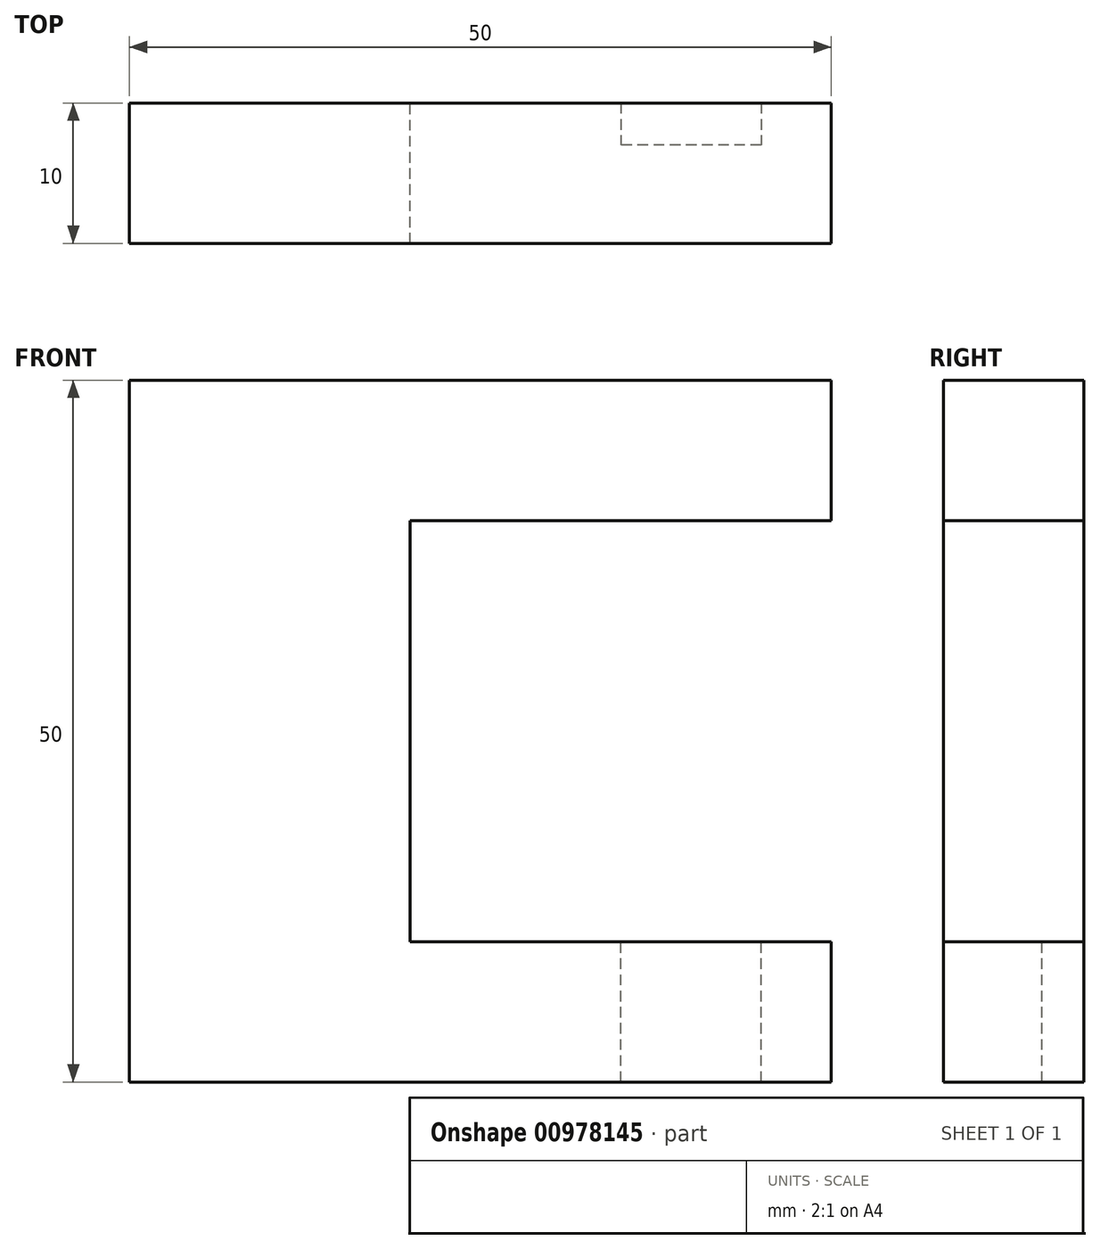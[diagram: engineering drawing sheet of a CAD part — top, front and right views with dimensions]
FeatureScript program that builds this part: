
annotation { "Feature Type Name" : "Feature", "Feature Type Description" : "" }
export const myFeature = defineFeature(function(context is Context, id is Id, definition is map)
    precondition{}
    {
        {
            var Q0;
            Q0=qCreatedBy(makeId("Front.planeOp"),FACE);
            var sketch = newSketch(context, id + "F0", { "sketchPlane" : qUnion([Q0])});
            skLineSegment(sketch, "E0.bottom", {"start": v(0, 0) * mm, "end": v(20, 0) * mm});
            skLineSegment(sketch, "E0.top", {"start": v(0, 50) * mm, "end": v(20, 50) * mm});
            skLineSegment(sketch, "E0.left", {"start": v(0, 0) * mm, "end": v(0, 50) * mm});
            skLineSegment(sketch, "E0.right", {"start": v(20, 10) * mm, "end": v(20, 40) * mm});
            skLineSegment(sketch, "E1.bottom", {"start": v(20, 0) * mm, "end": v(50, 0) * mm});
            skLineSegment(sketch, "E1.top", {"start": v(20, 10) * mm, "end": v(50, 10) * mm});
            skLineSegment(sketch, "E1.right", {"start": v(50, 0) * mm, "end": v(50, 10) * mm});
            skLineSegment(sketch, "E2.bottom", {"start": v(20, 50) * mm, "end": v(50, 50) * mm});
            skLineSegment(sketch, "E2.top", {"start": v(20, 40) * mm, "end": v(50, 40) * mm});
            skLineSegment(sketch, "E2.right", {"start": v(50, 50) * mm, "end": v(50, 40) * mm});
            skSolve(sketch);
        }
        {
            var Q0;
            Q0 = qSketchRegion(id + "F0", true);
            extrude(context, id + "F1", {"entities" : qUnion([Q0]), "depth" : 10 * mm, "offsetDistance" : 25 * mm});
        }
        {
            var Q0;
            Q0=makeQuery(id+"F1.opExtrude","SWEPT_FACE",FACE,{"disambiguationData":[OSD([sQuery(id+"F0.wireOp",EDGE,"E1.top")])]});
            var sketch = newSketch(context, id + "F2", { "sketchPlane" : qUnion([Q0])});
            skLineSegment(sketch, "E3.bottom", {"start": v(45, 0) * mm, "end": v(35, 0) * mm});
            skLineSegment(sketch, "E3.top", {"start": v(45, -3) * mm, "end": v(35, -3) * mm});
            skLineSegment(sketch, "E3.left", {"start": v(45, 0) * mm, "end": v(45, -3) * mm});
            skLineSegment(sketch, "E3.right", {"start": v(35, 0) * mm, "end": v(35, -3) * mm});
            skSolve(sketch);
        }
        {
            var Q0;
            Q0 = qSketchRegion(id + "F2", true);
            extrude(context, id + "F3", {"entities" : qUnion([Q0]), "operationType" : NewBodyOperationType.REMOVE, "oppositeDirection" : true, "depth" : 25 * mm, "offsetDistance" : 25 * mm});
        }
    });
